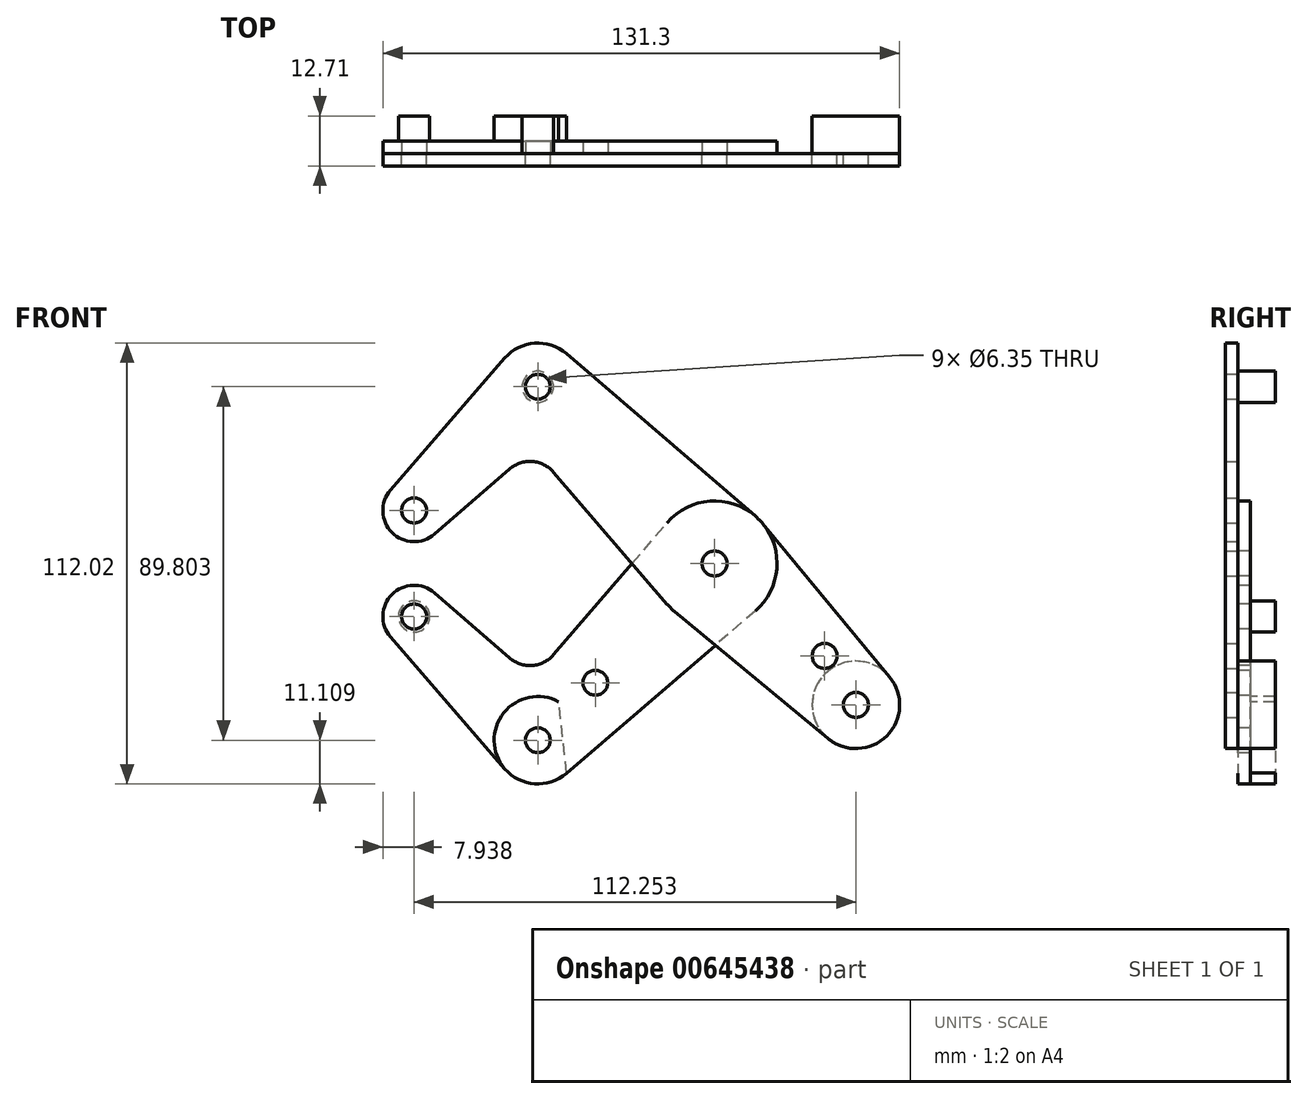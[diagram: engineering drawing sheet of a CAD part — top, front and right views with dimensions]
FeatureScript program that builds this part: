
annotation { "Feature Type Name" : "Feature", "Feature Type Description" : "" }
export const myFeature = defineFeature(function(context is Context, id is Id, definition is map)
    precondition{}
    {
        {
            var Q0;
            Q0=qCreatedBy(makeId("Front.planeOp"),FACE);
            var sketch = newSketch(context, id + "F0", { "sketchPlane" : qUnion([Q0])});
            skLineSegment(sketch, "E0", {"start": v(-76.33, 13.47) * mm, "end": v(-44.9, 44.9) * mm, "construction": true});
            skLineSegment(sketch, "E1", {"start": v(-44.9, 44.9) * mm, "end": v(35.92, -35.92) * mm, "construction": true});
            skCircle(sketch, "E2", {"center": v(-76.33, 13.47) * mm, "radius": 7.94 * mm});
            skCircle(sketch, "E3", {"center": v(-76.33, 13.47) * mm, "radius": 3.18 * mm});
            skCircle(sketch, "E4", {"center": v(-44.9, 44.9) * mm, "radius": 11.11 * mm});
            skCircle(sketch, "E5", {"center": v(-44.9, 44.9) * mm, "radius": 3.18 * mm});
            skCircle(sketch, "E6", {"center": v(0, 0) * mm, "radius": 15.88 * mm});
            skCircle(sketch, "E7", {"center": v(0, 0) * mm, "radius": 3.98 * mm});
            skCircle(sketch, "E8", {"center": v(0, 0) * mm, "radius": 3.18 * mm});
            skCircle(sketch, "E9", {"center": v(35.92, -35.92) * mm, "radius": 11.11 * mm});
            skCircle(sketch, "E10", {"center": v(35.92, -35.92) * mm, "radius": 3.18 * mm});
            skCircle(sketch, "E11", {"center": v(27.97, -23.48) * mm, "radius": 3.18 * mm});
            skLineSegment(sketch, "E12", {"start": v(-82.33, 18.67) * mm, "end": v(-53.3, 52.18) * mm});
            skLineSegment(sketch, "E13", {"start": v(-71.13, 7.47) * mm, "end": v(-52.08, 23.98) * mm});
            skLineSegment(sketch, "E14", {"start": v(-40.85, 23.15) * mm, "end": v(-12.04, -10.35) * mm});
            skLineSegment(sketch, "E15", {"start": v(-10.12, -12.23) * mm, "end": v(28.83, -44.48) * mm});
            skLineSegment(sketch, "E16", {"start": v(12.23, 10.12) * mm, "end": v(44.48, -28.83) * mm});
            skLineSegment(sketch, "E17", {"start": v(10.35, 12.04) * mm, "end": v(-37.66, 53.33) * mm});
            skArc(sketch, "E18.filletArc", {"start": v(-40.85, 23.15) * mm, "mid": v(-46.3, 25.9) * mm, "end": v(-52.08, 23.98) * mm});
            skLineSegment(sketch, "E19", {"start": v(0, 0) * mm, "end": v(-44.9, -44.9) * mm, "construction": true});
            skLineSegment(sketch, "E20", {"start": v(-44.9, -44.9) * mm, "end": v(-76.33, -13.47) * mm, "construction": true});
            skCircle(sketch, "E21", {"center": v(-76.33, -13.47) * mm, "radius": 7.94 * mm});
            skCircle(sketch, "E22", {"center": v(-76.33, -13.47) * mm, "radius": 3.18 * mm});
            skCircle(sketch, "E23", {"center": v(-44.9, -44.9) * mm, "radius": 11.11 * mm});
            skCircle(sketch, "E24", {"center": v(-44.9, -44.9) * mm, "radius": 3.18 * mm});
            skCircle(sketch, "E25", {"center": v(-30.3, -30.3) * mm, "radius": 3.18 * mm});
            skLineSegment(sketch, "E26", {"start": v(-82.33, -18.67) * mm, "end": v(-53.3, -52.18) * mm});
            skLineSegment(sketch, "E27", {"start": v(-40.85, -23.15) * mm, "end": v(-12.04, 10.35) * mm});
            skLineSegment(sketch, "E28", {"start": v(-71.13, -7.47) * mm, "end": v(-52.08, -23.98) * mm});
            skLineSegment(sketch, "E29", {"start": v(10.35, -12.04) * mm, "end": v(-37.66, -53.33) * mm});
            skArc(sketch, "E30.filletArc", {"start": v(-52.08, -23.98) * mm, "mid": v(-46.3, -25.9) * mm, "end": v(-40.85, -23.15) * mm});
            skSolve(sketch);
        }
        {
            var Q0;
            Q0=makeQuery(id+"F0.imprint","IMPRINT",FACE,{"disambiguationData":[TD([[makeQuery(id+"F0.imprint","IMPRINT",EDGE,{"derivedFrom":sQuery(id+"F0.wireOp",EDGE,"E3")}),-1.0]])]});
            var Q1;
            {var subQ0=sQuery(id+"F0.wireOp",EDGE,"E12");Q1=makeQuery(id+"F0.imprint","IMPRINT",FACE,{"disambiguationData":[TD([[makeQuery(id+"F0.imprint","IMPRINT",EDGE,{"derivedFrom":subQ0}),-1.0]])]});}
            var Q2;
            {var subQ0=sQuery(id+"F0.wireOp",EDGE,"E14");var subQ1=sQuery(id+"F0.wireOp",EDGE,"E6");var subQ2=makeQuery(id+"F0.imprint","INTERSECT",VERTEX,{"derivedFrom":[subQ1,subQ0]});Q2=makeQuery(id+"F0.imprint","IMPRINT",FACE,{"disambiguationData":[TD([[makeQuery(id+"F0.imprint","IMPRINT",EDGE,{"disambiguationData":[TD([[subQ2,1.0]])],"derivedFrom":subQ1}),-1.0]])]});}
            var Q3;
            {var subQ0=sQuery(id+"F0.wireOp",EDGE,"E15");var subQ1=sQuery(id+"F0.wireOp",EDGE,"E6");var subQ2=makeQuery(id+"F0.imprint","INTERSECT",VERTEX,{"derivedFrom":[subQ1,subQ0]});Q3=makeQuery(id+"F0.imprint","IMPRINT",FACE,{"disambiguationData":[TD([[makeQuery(id+"F0.imprint","IMPRINT",EDGE,{"disambiguationData":[TD([[subQ2,-1.0]])],"derivedFrom":subQ1}),-1.0]])]});}
            var Q4;
            Q4=makeQuery(id+"F0.imprint","IMPRINT",FACE,{"disambiguationData":[TD([[makeQuery(id+"F0.imprint","IMPRINT",EDGE,{"derivedFrom":sQuery(id+"F0.wireOp",EDGE,"E7")}),-1.0]])]});
            var Q5;
            Q5=makeQuery(id+"F0.imprint","IMPRINT",FACE,{"disambiguationData":[TD([[makeQuery(id+"F0.imprint","IMPRINT",EDGE,{"derivedFrom":sQuery(id+"F0.wireOp",EDGE,"E7")}),1.0]])]});
            var Q6;
            Q6=makeQuery(id+"F0.imprint","IMPRINT",FACE,{"disambiguationData":[TD([[makeQuery(id+"F0.imprint","IMPRINT",EDGE,{"derivedFrom":sQuery(id+"F0.wireOp",EDGE,"E11")}),-1.0]])]});
            var Q7;
            Q7=makeQuery(id+"F0.imprint","IMPRINT",FACE,{"disambiguationData":[TD([[makeQuery(id+"F0.imprint","IMPRINT",EDGE,{"derivedFrom":sQuery(id+"F0.wireOp",EDGE,"E10")}),-1.0]])]});
            var Q8;
            Q8=makeQuery(id+"F0.imprint","IMPRINT",FACE,{"disambiguationData":[TD([[makeQuery(id+"F0.imprint","IMPRINT",EDGE,{"derivedFrom":sQuery(id+"F0.wireOp",EDGE,"E5")}),-1.0]])]});
            extrude(context, id + "F1", {"entities" : qUnion([Q0, Q1, Q2, Q3, Q4, Q5, Q6, Q7, Q8]), "depth" : 3.17 * mm, "offsetDistance" : 25.4 * mm});
        }
        {
            var Q0;
            Q0=makeQuery(id+"F0.imprint","IMPRINT",FACE,{"disambiguationData":[TD([[makeQuery(id+"F0.imprint","IMPRINT",EDGE,{"derivedFrom":sQuery(id+"F0.wireOp",EDGE,"E22")}),-1.0]])]});
            var Q1;
            Q1=makeQuery(id+"F0.imprint","IMPRINT",FACE,{"disambiguationData":[TD([[makeQuery(id+"F0.imprint","IMPRINT",EDGE,{"derivedFrom":sQuery(id+"F0.wireOp",EDGE,"E25")}),-1.0]])]});
            var Q2;
            Q2=makeQuery(id+"F0.imprint","IMPRINT",FACE,{"disambiguationData":[TD([[makeQuery(id+"F0.imprint","IMPRINT",EDGE,{"derivedFrom":sQuery(id+"F0.wireOp",EDGE,"E24")}),-1.0]])]});
            var Q3;
            {var subQ0=sQuery(id+"F0.wireOp",EDGE,"E15");var subQ1=sQuery(id+"F0.wireOp",EDGE,"E6");var subQ2=makeQuery(id+"F0.imprint","INTERSECT",VERTEX,{"derivedFrom":[subQ1,subQ0]});Q3=makeQuery(id+"F0.imprint","IMPRINT",FACE,{"disambiguationData":[TD([[makeQuery(id+"F0.imprint","IMPRINT",EDGE,{"disambiguationData":[TD([[subQ2,-1.0]])],"derivedFrom":subQ1}),-1.0]])]});}
            var Q4;
            {var subQ0=sQuery(id+"F0.wireOp",EDGE,"E14");var subQ1=sQuery(id+"F0.wireOp",EDGE,"E6");var subQ2=makeQuery(id+"F0.imprint","INTERSECT",VERTEX,{"derivedFrom":[subQ1,subQ0]});Q4=makeQuery(id+"F0.imprint","IMPRINT",FACE,{"disambiguationData":[TD([[makeQuery(id+"F0.imprint","IMPRINT",EDGE,{"disambiguationData":[TD([[subQ2,1.0]])],"derivedFrom":subQ1}),-1.0]])]});}
            var Q5;
            Q5=makeQuery(id+"F0.imprint","IMPRINT",FACE,{"disambiguationData":[TD([[makeQuery(id+"F0.imprint","IMPRINT",EDGE,{"derivedFrom":sQuery(id+"F0.wireOp",EDGE,"E7")}),-1.0]])]});
            var Q6;
            Q6=makeQuery(id+"F0.imprint","IMPRINT",FACE,{"disambiguationData":[TD([[makeQuery(id+"F0.imprint","IMPRINT",EDGE,{"derivedFrom":sQuery(id+"F0.wireOp",EDGE,"E7")}),1.0]])]});
            extrude(context, id + "F2", {"entities" : qUnion([Q0, Q1, Q2, Q3, Q4, Q5, Q6]), "oppositeDirection" : true, "depth" : 3.17 * mm, "offsetDistance" : 25.4 * mm});
        }
        {
            var Q0;
            Q0=makeQuery(id+"F1.opExtrude","CAP_FACE",FACE,{"disambiguationData":[OSD([sQuery(id+"F0.wireOp",EDGE,"E2"),sQuery(id+"F0.wireOp",EDGE,"E3"),sQuery(id+"F0.wireOp",EDGE,"E4"),sQuery(id+"F0.wireOp",EDGE,"E5"),sQuery(id+"F0.wireOp",EDGE,"E6"),sQuery(id+"F0.wireOp",EDGE,"E8"),sQuery(id+"F0.wireOp",EDGE,"E9"),sQuery(id+"F0.wireOp",EDGE,"E10"),sQuery(id+"F0.wireOp",EDGE,"E11"),sQuery(id+"F0.wireOp",EDGE,"E12"),sQuery(id+"F0.wireOp",EDGE,"E13"),sQuery(id+"F0.wireOp",EDGE,"E14"),sQuery(id+"F0.wireOp",EDGE,"E15"),sQuery(id+"F0.wireOp",EDGE,"E16"),sQuery(id+"F0.wireOp",EDGE,"E17"),sQuery(id+"F0.wireOp",EDGE,"E18.filletArc")])],"isStart":false});
            var sketch = newSketch(context, id + "F3", { "sketchPlane" : qUnion([Q0])});
            skCircle(sketch, "E31", {"center": v(-44.9, 44.9) * mm, "radius": 3.98 * mm});
            skCircle(sketch, "E32.0", {"center": v(35.92, -35.92) * mm, "radius": 11.11 * mm});
            skSolve(sketch);
        }
        {
            var Q0;
            Q0=makeQuery(id+"F0.imprint","IMPRINT",FACE,{"disambiguationData":[TD([[makeQuery(id+"F0.imprint","IMPRINT",EDGE,{"derivedFrom":sQuery(id+"F0.wireOp",EDGE,"E25")}),-1.0]])]});
            var sketch = newSketch(context, id + "F4", { "sketchPlane" : qUnion([Q0])});
            skCircle(sketch, "E33", {"center": v(-76.33, -13.47) * mm, "radius": 3.98 * mm});
            skArc(sketch, "E34.0", {"start": v(-39.6, -35.14) * mm, "mid": v(-55.95, -46.13) * mm, "end": v(-37.58, -53.26) * mm});
            skLineSegment(sketch, "E35", {"start": v(-44.9, -44.9) * mm, "end": v(35.92, -35.92) * mm, "construction": true});
            skLineSegment(sketch, "E36", {"start": v(-39.6, -35.14) * mm, "end": v(-37.58, -53.26) * mm});
            skSolve(sketch);
        }
        {
            var Q0;
            Q0=qCreatedBy(makeId("Front.planeOp"),FACE);
            cPlane(context, id + "F5", {"entities" : qUnion([Q0]), "cplaneType" : CPlaneType.OFFSET, "offset" : 9.52 * mm, "oppositeDirection" : true, "width" : 152.4 * mm, "height" : 152.4 * mm});
        }
        {
            var Q0;
            Q0 = qSketchRegion(id + "F3", true);
            var Q1;
            Q1 = qSketchRegion(id + "F4", true);
            var Q2;
            Q2=qCreatedBy(id+"F5.planeOp",FACE);
            extrude(context, id + "F6", {"entities" : qUnion([Q0, Q1]), "endBound" : BoundingType.UP_TO_SURFACE, "oppositeDirection" : true, "depth" : 25.4 * mm, "endBoundEntityFace" : qUnion([Q2]), "offsetDistance" : 25.4 * mm});
        }
        {
            var Q0;
            Q0=makeQuery(id+"F2.opExtrude","SWEPT_BODY",BODY,{"disambiguationData":[OSD([sQuery(id+"F0.wireOp",EDGE,"E6"),sQuery(id+"F0.wireOp",EDGE,"E8"),sQuery(id+"F0.wireOp",EDGE,"E21"),sQuery(id+"F0.wireOp",EDGE,"E22"),sQuery(id+"F0.wireOp",EDGE,"E23"),sQuery(id+"F0.wireOp",EDGE,"E24"),sQuery(id+"F0.wireOp",EDGE,"E25"),sQuery(id+"F0.wireOp",EDGE,"E26"),sQuery(id+"F0.wireOp",EDGE,"E27"),sQuery(id+"F0.wireOp",EDGE,"E28"),sQuery(id+"F0.wireOp",EDGE,"E29"),sQuery(id+"F0.wireOp",EDGE,"E30.filletArc")])]});
            var Q1;
            Q1=makeQuery(id+"F1.opExtrude","SWEPT_BODY",BODY,{"disambiguationData":[OSD([sQuery(id+"F0.wireOp",EDGE,"E2"),sQuery(id+"F0.wireOp",EDGE,"E3"),sQuery(id+"F0.wireOp",EDGE,"E4"),sQuery(id+"F0.wireOp",EDGE,"E5"),sQuery(id+"F0.wireOp",EDGE,"E6"),sQuery(id+"F0.wireOp",EDGE,"E8"),sQuery(id+"F0.wireOp",EDGE,"E9"),sQuery(id+"F0.wireOp",EDGE,"E10"),sQuery(id+"F0.wireOp",EDGE,"E11"),sQuery(id+"F0.wireOp",EDGE,"E12"),sQuery(id+"F0.wireOp",EDGE,"E13"),sQuery(id+"F0.wireOp",EDGE,"E14"),sQuery(id+"F0.wireOp",EDGE,"E15"),sQuery(id+"F0.wireOp",EDGE,"E16"),sQuery(id+"F0.wireOp",EDGE,"E17"),sQuery(id+"F0.wireOp",EDGE,"E18.filletArc")])]});
            var Q2;
            Q2=makeQuery(id+"F6.opExtrude","SWEPT_BODY",BODY,{"disambiguationData":[OSD([sQuery(id+"F3.wireOp",EDGE,"E32.0")])]});
            var Q3;
            Q3=makeQuery(id+"F6.opExtrude","SWEPT_BODY",BODY,{"disambiguationData":[OSD([sQuery(id+"F3.wireOp",EDGE,"E31")])]});
            var Q4;
            Q4=makeQuery(id+"F6.opExtrude","SWEPT_BODY",BODY,{"disambiguationData":[OSD([sQuery(id+"F4.wireOp",EDGE,"E33")])]});
            var Q5;
            Q5=makeQuery(id+"F6.opExtrude","SWEPT_BODY",BODY,{"disambiguationData":[OSD([sQuery(id+"F4.wireOp",EDGE,"E34.0"),sQuery(id+"F4.wireOp",EDGE,"E36")])]});
            booleanBodies(context, id + "F7", {"operationType" : BooleanOperationType.SUBTRACTION, "tools" : qUnion([Q0, Q1]), "targets" : qUnion([Q2, Q3, Q4, Q5]), "keepTools" : true});
        }
    });
